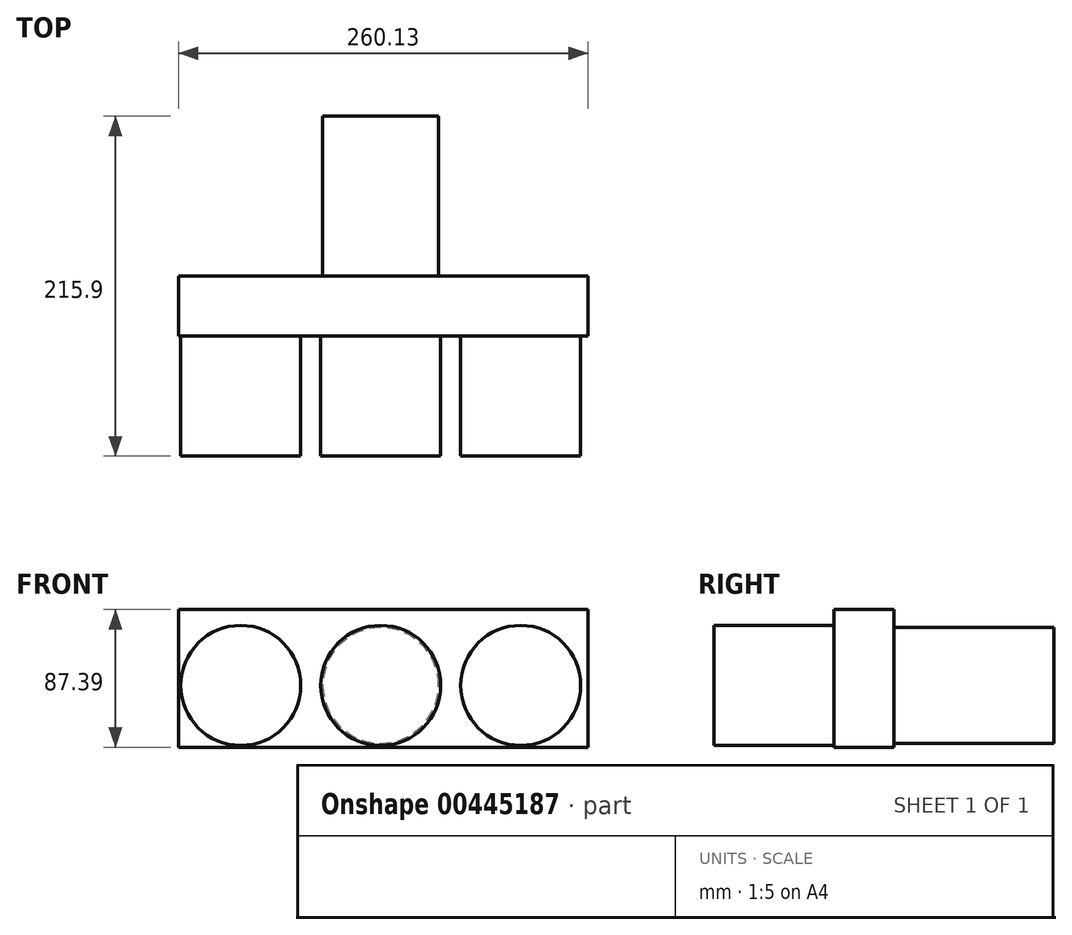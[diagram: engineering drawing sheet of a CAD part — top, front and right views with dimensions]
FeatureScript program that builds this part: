
annotation { "Feature Type Name" : "Feature", "Feature Type Description" : "" }
export const myFeature = defineFeature(function(context is Context, id is Id, definition is map)
    precondition{}
    {
        {
            var Q0;
            Q0=qCreatedBy(makeId("Front.planeOp"),FACE);
            var sketch = newSketch(context, id + "F0", { "sketchPlane" : qUnion([Q0])});
            skCircle(sketch, "E0", {"center": v(0, 0) * mm, "radius": 38.1 * mm});
            skLineSegment(sketch, "E1", {"start": v(-38.1, 0) * mm, "end": v(-88.9, 0) * mm});
            skCircle(sketch, "E2", {"center": v(-88.9, 0) * mm, "radius": 38.1 * mm});
            skLineSegment(sketch, "E3", {"start": v(38.1, 0) * mm, "end": v(88.9, 0) * mm});
            skCircle(sketch, "E4", {"center": v(88.9, 0) * mm, "radius": 38.1 * mm});
            skSolve(sketch);
        }
        {
            var Q0;
            Q0 = qSketchRegion(id + "F0", true);
            extrude(context, id + "F1", {"entities" : qUnion([Q0]), "depth" : 76.2 * mm});
        }
        {
            var Q0;
            Q0=qCreatedBy(makeId("Front.planeOp"),FACE);
            var sketch = newSketch(context, id + "F2", { "sketchPlane" : qUnion([Q0])});
            skLineSegment(sketch, "E5.bottom", {"start": v(-128.5, -39.27) * mm, "end": v(131.63, -39.27) * mm});
            skLineSegment(sketch, "E5.top", {"start": v(-128.5, 48.12) * mm, "end": v(131.63, 48.12) * mm});
            skLineSegment(sketch, "E5.left", {"start": v(-128.5, -39.27) * mm, "end": v(-128.5, 48.12) * mm});
            skLineSegment(sketch, "E5.right", {"start": v(131.63, -39.27) * mm, "end": v(131.63, 48.12) * mm});
            skSolve(sketch);
        }
        {
            var Q0;
            Q0 = qSketchRegion(id + "F2", true);
            extrude(context, id + "F3", {"entities" : qUnion([Q0]), "oppositeDirection" : true, "depth" : 38.1 * mm});
        }
        {
            var Q0;
            Q0=makeQuery(id+"F3.opExtrude","CAP_FACE",FACE,{"disambiguationData":[OSD([sQuery(id+"F2.wireOp",EDGE,"E5.bottom"),sQuery(id+"F2.wireOp",EDGE,"E5.top"),sQuery(id+"F2.wireOp",EDGE,"E5.left"),sQuery(id+"F2.wireOp",EDGE,"E5.right")])],"isStart":false});
            var sketch = newSketch(context, id + "F4", { "sketchPlane" : qUnion([Q0])});
            skCircle(sketch, "E6", {"center": v(0, 0) * mm, "radius": 36.77 * mm});
            skSolve(sketch);
        }
        {
            var Q0;
            Q0 = qSketchRegion(id + "F4", true);
            extrude(context, id + "F5", {"entities" : qUnion([Q0]), "operationType" : NewBodyOperationType.ADD, "depth" : 101.6 * mm});
        }
    });
